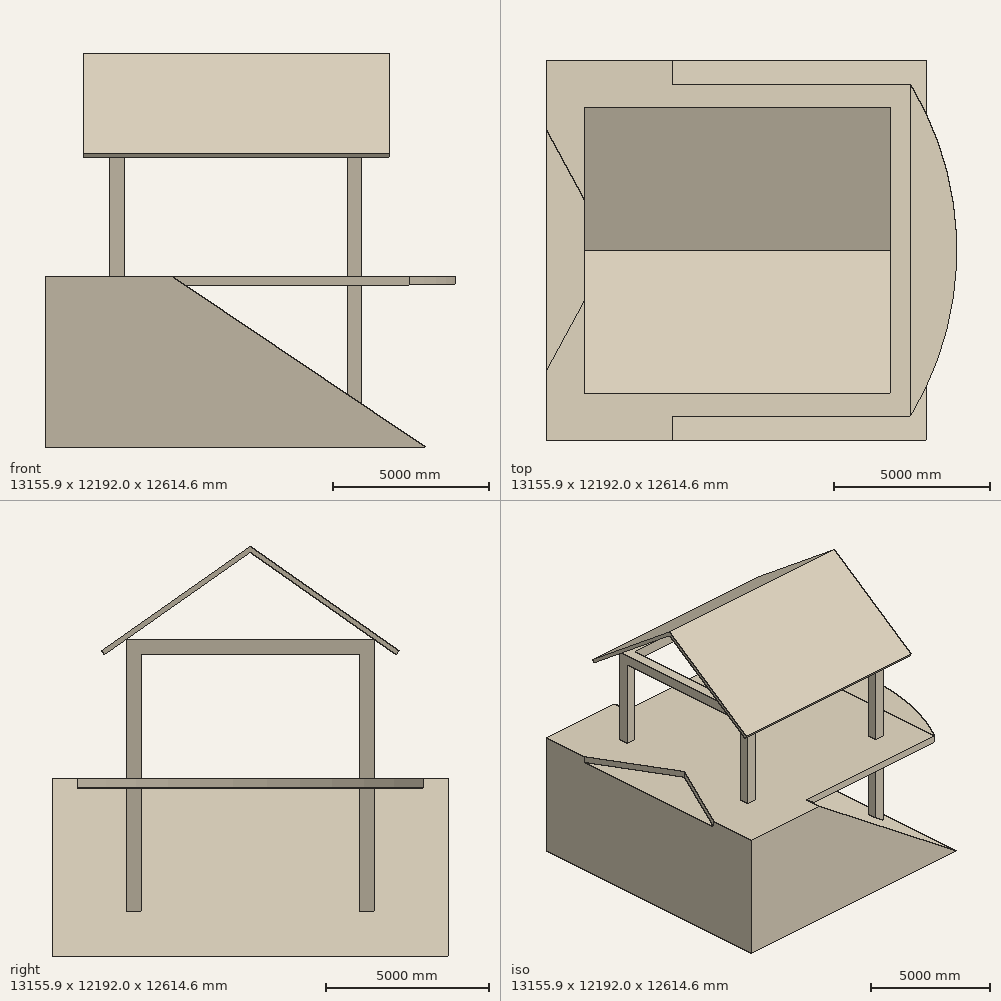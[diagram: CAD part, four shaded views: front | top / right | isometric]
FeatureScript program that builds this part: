
annotation { "Feature Type Name" : "Feature", "Feature Type Description" : "" }
export const myFeature = defineFeature(function(context is Context, id is Id, definition is map)
    precondition{}
    {
        {
            var Q0;
            Q0=qCreatedBy(makeId("Front.planeOp"),FACE);
            var sketch = newSketch(context, id + "F0", { "sketchPlane" : qUnion([Q0])});
            skLineSegment(sketch, "E0", {"start": v(-4044.06, 0) * mm, "end": v(0, 0) * mm});
            skLineSegment(sketch, "E1", {"start": v(0, 0) * mm, "end": v(8147.94, -5486.4) * mm});
            skLineSegment(sketch, "E2", {"start": v(8147.94, -5486.4) * mm, "end": v(-4044.06, -5486.4) * mm});
            skLineSegment(sketch, "E3", {"start": v(-4044.06, -5486.4) * mm, "end": v(-4044.06, 0) * mm});
            skSolve(sketch);
        }
        {
            var Q0;
            Q0=qSketchRegion(id+"F0",true);
            extrude(context, id + "F1", {"entities" : qUnion([Q0]), "endBound" : BoundingType.SYMMETRIC, "depth" : 12192 * mm});
        }
        {
            var Q0;
            Q0=qCreatedBy(makeId("Top.planeOp"),FACE);
            var sketch = newSketch(context, id + "F2", { "sketchPlane" : qUnion([Q0])});
            skLineSegment(sketch, "E4.bottom", {"start": v(-3048, 5334) * mm, "end": v(7620, 5334) * mm});
            skLineSegment(sketch, "E4.top", {"start": v(-3048, -5334) * mm, "end": v(7620, -5334) * mm});
            skLineSegment(sketch, "E4.left", {"start": v(-3048, 5334) * mm, "end": v(-3048, -5334) * mm});
            skLineSegment(sketch, "E4.right", {"start": v(7620, 5334) * mm, "end": v(7620, -5334) * mm});
            skSolve(sketch);
        }
        {
            var Q0;
            Q0=qSketchRegion(id+"F2",true);
            extrude(context, id + "F3", {"entities" : qUnion([Q0]), "operationType" : NewBodyOperationType.ADD, "oppositeDirection" : true, "depth" : 304.8 * mm});
        }
        {
            var Q0;
            Q0=makeQuery(id+"F3.boolean.opBoolean","MERGE",FACE,{"derivedFrom":[makeQuery(id+"F1.opExtrude","SWEPT_FACE",FACE,{"disambiguationData":[OSD([sQuery(id+"F0.wireOp",EDGE,"E0")])]}),makeQuery(id+"F3.opExtrude","CAP_FACE",FACE,{"disambiguationData":[OSD([sQuery(id+"F2.wireOp",EDGE,"E4.bottom"),sQuery(id+"F2.wireOp",EDGE,"E4.top"),sQuery(id+"F2.wireOp",EDGE,"E4.left"),sQuery(id+"F2.wireOp",EDGE,"E4.right")])],"isStart":true})]});
            var sketch = newSketch(context, id + "F4", { "sketchPlane" : qUnion([Q0])});
            skLineSegment(sketch, "E5.bottom", {"start": v(5638.8, 3810) * mm, "end": v(6096, 3810) * mm});
            skLineSegment(sketch, "E5.top", {"start": v(5638.8, 3352.8) * mm, "end": v(6096, 3352.8) * mm});
            skLineSegment(sketch, "E5.left", {"start": v(5638.8, 3810) * mm, "end": v(5638.8, 3352.8) * mm});
            skLineSegment(sketch, "E5.right", {"start": v(6096, 3810) * mm, "end": v(6096, 3352.8) * mm});
            skLineSegment(sketch, "E6.bottom", {"start": v(5638.8, -3352.8) * mm, "end": v(6096, -3352.8) * mm});
            skLineSegment(sketch, "E6.top", {"start": v(5638.8, -3810) * mm, "end": v(6096, -3810) * mm});
            skLineSegment(sketch, "E6.left", {"start": v(5638.8, -3352.8) * mm, "end": v(5638.8, -3810) * mm});
            skLineSegment(sketch, "E6.right", {"start": v(6096, -3352.8) * mm, "end": v(6096, -3810) * mm});
            skLineSegment(sketch, "E7.bottom", {"start": v(-1981.2, -3352.8) * mm, "end": v(-1524, -3352.8) * mm});
            skLineSegment(sketch, "E7.top", {"start": v(-1981.2, -3810) * mm, "end": v(-1524, -3810) * mm});
            skLineSegment(sketch, "E7.left", {"start": v(-1981.2, -3352.8) * mm, "end": v(-1981.2, -3810) * mm});
            skLineSegment(sketch, "E7.right", {"start": v(-1524, -3352.8) * mm, "end": v(-1524, -3810) * mm});
            skLineSegment(sketch, "E8.bottom", {"start": v(-1981.2, 3352.8) * mm, "end": v(-1524, 3352.8) * mm});
            skLineSegment(sketch, "E8.top", {"start": v(-1981.2, 3810) * mm, "end": v(-1524, 3810) * mm});
            skLineSegment(sketch, "E8.left", {"start": v(-1981.2, 3352.8) * mm, "end": v(-1981.2, 3810) * mm});
            skLineSegment(sketch, "E8.right", {"start": v(-1524, 3352.8) * mm, "end": v(-1524, 3810) * mm});
            skSolve(sketch);
        }
        {
            var Q0;
            Q0=qSketchRegion(id+"F4",true);
            extrude(context, id + "F5", {"entities" : qUnion([Q0]), "operationType" : NewBodyOperationType.ADD, "endBound" : BoundingType.SYMMETRIC, "depth" : 8534.4 * mm});
        }
        {
            var Q0;
            Q0=makeQuery(id+"F5.opExtrude","SWEPT_FACE",FACE,{"disambiguationData":[OSD([sQuery(id+"F4.wireOp",EDGE,"E8.bottom")])]});
            var sketch = newSketch(context, id + "F6", { "sketchPlane" : qUnion([Q0])});
            skLineSegment(sketch, "E9.bottom", {"start": v(-1981.2, 4267.2) * mm, "end": v(-1524, 4267.2) * mm});
            skLineSegment(sketch, "E9.top", {"start": v(-1981.2, 3810) * mm, "end": v(-1524, 3810) * mm});
            skLineSegment(sketch, "E9.left", {"start": v(-1981.2, 4267.2) * mm, "end": v(-1981.2, 3810) * mm});
            skLineSegment(sketch, "E9.right", {"start": v(-1524, 4267.2) * mm, "end": v(-1524, 3810) * mm});
            skLineSegment(sketch, "E10.bottom", {"start": v(6096, 4267.2) * mm, "end": v(5638.8, 4267.2) * mm});
            skLineSegment(sketch, "E10.top", {"start": v(6096, 3810) * mm, "end": v(5638.8, 3810) * mm});
            skLineSegment(sketch, "E10.left", {"start": v(6096, 4267.2) * mm, "end": v(6096, 3810) * mm});
            skLineSegment(sketch, "E10.right", {"start": v(5638.8, 4267.2) * mm, "end": v(5638.8, 3810) * mm});
            skSolve(sketch);
        }
        {
            var Q0;
            Q0=qSketchRegion(id+"F6",true);
            extrude(context, id + "F7", {"entities" : qUnion([Q0]), "operationType" : NewBodyOperationType.ADD, "depth" : 7112 * mm});
        }
        {
            var Q0;
            {var subQ2=sQuery(id+"F4.wireOp",EDGE,"E6.left");var subQ4=makeQuery(id+"F1.opExtrude","SWEPT_FACE",FACE,{"disambiguationData":[OSD([sQuery(id+"F0.wireOp",EDGE,"E0")])]});var subQ6=sQuery(id+"F4.wireOp",EDGE,"E5.left");Q0=makeQuery(id+"F7.boolean.opBoolean","MERGE",FACE,{"derivedFrom":[makeQuery(id+"F5.boolean.opBoolean","SPLIT",FACE,{"disambiguationData":[TD([subQ4])],"derivedFrom":makeQuery(id+"F5.opExtrude","SWEPT_FACE",FACE,{"disambiguationData":[OSD([subQ6])]})}),makeQuery(id+"F5.boolean.opBoolean","SPLIT",FACE,{"disambiguationData":[TD([subQ4])],"derivedFrom":makeQuery(id+"F5.opExtrude","SWEPT_FACE",FACE,{"disambiguationData":[OSD([subQ2])]})}),makeQuery(id+"F7.opExtrude","SWEPT_FACE",FACE,{"disambiguationData":[OSD([sQuery(id+"F6.wireOp",EDGE,"E10.right")])]})]});}
            var sketch = newSketch(context, id + "F8", { "sketchPlane" : qUnion([Q0])});
            skLineSegment(sketch, "E11.bottom", {"start": v(-3810, 4267.2) * mm, "end": v(-3352.8, 4267.2) * mm});
            skLineSegment(sketch, "E11.top", {"start": v(-3810, 3810) * mm, "end": v(-3352.8, 3810) * mm});
            skLineSegment(sketch, "E11.left", {"start": v(-3810, 4267.2) * mm, "end": v(-3810, 3810) * mm});
            skLineSegment(sketch, "E11.right", {"start": v(-3352.8, 4267.2) * mm, "end": v(-3352.8, 3810) * mm});
            skLineSegment(sketch, "E12.bottom", {"start": v(3352.8, 3810) * mm, "end": v(3810, 3810) * mm});
            skLineSegment(sketch, "E12.top", {"start": v(3352.8, 4267.2) * mm, "end": v(3810, 4267.2) * mm});
            skLineSegment(sketch, "E12.left", {"start": v(3352.8, 3810) * mm, "end": v(3352.8, 4267.2) * mm});
            skLineSegment(sketch, "E12.right", {"start": v(3810, 3810) * mm, "end": v(3810, 4267.2) * mm});
            skSolve(sketch);
        }
        {
            var Q0;
            Q0=qSketchRegion(id+"F8",true);
            extrude(context, id + "F9", {"entities" : qUnion([Q0]), "operationType" : NewBodyOperationType.ADD, "depth" : 7594.6 * mm});
        }
        {
            var Q0;
            Q0=qCreatedBy(makeId("Right.planeOp"),FACE);
            var sketch = newSketch(context, id + "F10", { "sketchPlane" : qUnion([Q0])});
            skLineSegment(sketch, "E13", {"start": v(-3810, 4267.2) * mm, "end": v(0, 6942) * mm});
            skLineSegment(sketch, "E14", {"start": v(0, 6942) * mm, "end": v(0, 7128.2) * mm});
            skLineSegment(sketch, "E15", {"start": v(0, 7128.2) * mm, "end": v(-4576.9, 3915) * mm});
            skLineSegment(sketch, "E16", {"start": v(-4576.9, 3915) * mm, "end": v(-4489.34, 3790.27) * mm});
            skLineSegment(sketch, "E17", {"start": v(-4489.34, 3790.27) * mm, "end": v(-3810, 4267.2) * mm});
            skLineSegment(sketch, "E18.MirrorCS", {"start": v(0, 7128.2) * mm, "end": v(4576.9, 3915) * mm});
            skLineSegment(sketch, "E19.MirrorCS", {"start": v(3810, 4267.2) * mm, "end": v(0, 6942) * mm});
            skLineSegment(sketch, "E20.MirrorCS", {"start": v(4489.34, 3790.27) * mm, "end": v(3810, 4267.2) * mm});
            skLineSegment(sketch, "E21.MirrorCS", {"start": v(4576.9, 3915) * mm, "end": v(4489.34, 3790.27) * mm});
            skSolve(sketch);
        }
        {
            var Q0;
            Q0=qSketchRegion(id+"F10",true);
            extrude(context, id + "F11", {"entities" : qUnion([Q0]), "depth" : 6985 * mm, "hasSecondDirection" : true, "secondDirectionOppositeDirection" : true, "secondDirectionDepth" : 2819.4 * mm});
        }
        {
            var Q0;
            Q0=makeQuery(id+"F3.opExtrude","SWEPT_FACE",FACE,{"disambiguationData":[OSD([sQuery(id+"F2.wireOp",EDGE,"E4.right")])]});
            var sketch = newSketch(context, id + "F12", { "sketchPlane" : qUnion([Q0])});
            skLineSegment(sketch, "E22.bottom", {"start": v(-5334, -304.8) * mm, "end": v(-5283.2, -304.8) * mm});
            skLineSegment(sketch, "E22.top", {"start": v(-5334, 914.4) * mm, "end": v(-5283.2, 914.4) * mm});
            skLineSegment(sketch, "E22.left", {"start": v(-5334, -304.8) * mm, "end": v(-5334, 914.4) * mm});
            skLineSegment(sketch, "E22.right", {"start": v(-5283.2, -304.8) * mm, "end": v(-5283.2, 914.4) * mm});
            skLineSegment(sketch, "E23.1.0.0", {"start": v(-5060.95, -304.8) * mm, "end": v(-5060.95, 914.4) * mm});
            skLineSegment(sketch, "E23.1.0.1", {"start": v(-5010.15, -304.8) * mm, "end": v(-5010.15, 914.4) * mm});
            skLineSegment(sketch, "E23.1.0.2", {"start": v(-5060.95, 914.4) * mm, "end": v(-5010.15, 914.4) * mm});
            skLineSegment(sketch, "E23.1.0.3", {"start": v(-5060.95, -304.8) * mm, "end": v(-5010.15, -304.8) * mm});
            skLineSegment(sketch, "E23.2.0.0", {"start": v(-4787.9, -304.8) * mm, "end": v(-4787.9, 914.4) * mm});
            skLineSegment(sketch, "E23.2.0.1", {"start": v(-4737.1, -304.8) * mm, "end": v(-4737.1, 914.4) * mm});
            skLineSegment(sketch, "E23.2.0.2", {"start": v(-4787.9, 914.4) * mm, "end": v(-4737.1, 914.4) * mm});
            skLineSegment(sketch, "E23.2.0.3", {"start": v(-4787.9, -304.8) * mm, "end": v(-4737.1, -304.8) * mm});
            skLineSegment(sketch, "E23.3.0.0", {"start": v(-4514.85, -304.8) * mm, "end": v(-4514.85, 914.4) * mm});
            skLineSegment(sketch, "E23.3.0.1", {"start": v(-4464.05, -304.8) * mm, "end": v(-4464.05, 914.4) * mm});
            skLineSegment(sketch, "E23.3.0.2", {"start": v(-4514.85, 914.4) * mm, "end": v(-4464.05, 914.4) * mm});
            skLineSegment(sketch, "E23.3.0.3", {"start": v(-4514.85, -304.8) * mm, "end": v(-4464.05, -304.8) * mm});
            skLineSegment(sketch, "E23.4.0.0", {"start": v(-4241.8, -304.8) * mm, "end": v(-4241.8, 914.4) * mm});
            skLineSegment(sketch, "E23.4.0.1", {"start": v(-4191, -304.8) * mm, "end": v(-4191, 914.4) * mm});
            skLineSegment(sketch, "E23.4.0.2", {"start": v(-4241.8, 914.4) * mm, "end": v(-4191, 914.4) * mm});
            skLineSegment(sketch, "E23.4.0.3", {"start": v(-4241.8, -304.8) * mm, "end": v(-4191, -304.8) * mm});
            skLineSegment(sketch, "E23.5.0.0", {"start": v(-3968.75, -304.8) * mm, "end": v(-3968.75, 914.4) * mm});
            skLineSegment(sketch, "E23.5.0.1", {"start": v(-3917.95, -304.8) * mm, "end": v(-3917.95, 914.4) * mm});
            skLineSegment(sketch, "E23.5.0.2", {"start": v(-3968.75, 914.4) * mm, "end": v(-3917.95, 914.4) * mm});
            skLineSegment(sketch, "E23.5.0.3", {"start": v(-3968.75, -304.8) * mm, "end": v(-3917.95, -304.8) * mm});
            skLineSegment(sketch, "E23.6.0.0", {"start": v(-3695.7, -304.8) * mm, "end": v(-3695.7, 914.4) * mm});
            skLineSegment(sketch, "E23.6.0.1", {"start": v(-3644.9, -304.8) * mm, "end": v(-3644.9, 914.4) * mm});
            skLineSegment(sketch, "E23.6.0.2", {"start": v(-3695.7, 914.4) * mm, "end": v(-3644.9, 914.4) * mm});
            skLineSegment(sketch, "E23.6.0.3", {"start": v(-3695.7, -304.8) * mm, "end": v(-3644.9, -304.8) * mm});
            skLineSegment(sketch, "E23.7.0.0", {"start": v(-3422.65, -304.8) * mm, "end": v(-3422.65, 914.4) * mm});
            skLineSegment(sketch, "E23.7.0.1", {"start": v(-3371.85, -304.8) * mm, "end": v(-3371.85, 914.4) * mm});
            skLineSegment(sketch, "E23.7.0.2", {"start": v(-3422.65, 914.4) * mm, "end": v(-3371.85, 914.4) * mm});
            skLineSegment(sketch, "E23.7.0.3", {"start": v(-3422.65, -304.8) * mm, "end": v(-3371.85, -304.8) * mm});
            skLineSegment(sketch, "E23.8.0.0", {"start": v(-3149.6, -304.8) * mm, "end": v(-3149.6, 914.4) * mm});
            skLineSegment(sketch, "E23.8.0.1", {"start": v(-3098.8, -304.8) * mm, "end": v(-3098.8, 914.4) * mm});
            skLineSegment(sketch, "E23.8.0.2", {"start": v(-3149.6, 914.4) * mm, "end": v(-3098.8, 914.4) * mm});
            skLineSegment(sketch, "E23.8.0.3", {"start": v(-3149.6, -304.8) * mm, "end": v(-3098.8, -304.8) * mm});
            skLineSegment(sketch, "E23.9.0.0", {"start": v(-2876.55, -304.8) * mm, "end": v(-2876.55, 914.4) * mm});
            skLineSegment(sketch, "E23.9.0.1", {"start": v(-2825.75, -304.8) * mm, "end": v(-2825.75, 914.4) * mm});
            skLineSegment(sketch, "E23.9.0.2", {"start": v(-2876.55, 914.4) * mm, "end": v(-2825.75, 914.4) * mm});
            skLineSegment(sketch, "E23.9.0.3", {"start": v(-2876.55, -304.8) * mm, "end": v(-2825.75, -304.8) * mm});
            skLineSegment(sketch, "E23.10.0.0", {"start": v(-2603.5, -304.8) * mm, "end": v(-2603.5, 914.4) * mm});
            skLineSegment(sketch, "E23.10.0.1", {"start": v(-2552.7, -304.8) * mm, "end": v(-2552.7, 914.4) * mm});
            skLineSegment(sketch, "E23.10.0.2", {"start": v(-2603.5, 914.4) * mm, "end": v(-2552.7, 914.4) * mm});
            skLineSegment(sketch, "E23.10.0.3", {"start": v(-2603.5, -304.8) * mm, "end": v(-2552.7, -304.8) * mm});
            skLineSegment(sketch, "E23.11.0.0", {"start": v(-2330.45, -304.8) * mm, "end": v(-2330.45, 914.4) * mm});
            skLineSegment(sketch, "E23.11.0.1", {"start": v(-2279.65, -304.8) * mm, "end": v(-2279.65, 914.4) * mm});
            skLineSegment(sketch, "E23.11.0.2", {"start": v(-2330.45, 914.4) * mm, "end": v(-2279.65, 914.4) * mm});
            skLineSegment(sketch, "E23.11.0.3", {"start": v(-2330.45, -304.8) * mm, "end": v(-2279.65, -304.8) * mm});
            skLineSegment(sketch, "E23.12.0.0", {"start": v(-2057.4, -304.8) * mm, "end": v(-2057.4, 914.4) * mm});
            skLineSegment(sketch, "E23.12.0.1", {"start": v(-2006.6, -304.8) * mm, "end": v(-2006.6, 914.4) * mm});
            skLineSegment(sketch, "E23.12.0.2", {"start": v(-2057.4, 914.4) * mm, "end": v(-2006.6, 914.4) * mm});
            skLineSegment(sketch, "E23.12.0.3", {"start": v(-2057.4, -304.8) * mm, "end": v(-2006.6, -304.8) * mm});
            skLineSegment(sketch, "E23.13.0.0", {"start": v(-1784.35, -304.8) * mm, "end": v(-1784.35, 914.4) * mm});
            skLineSegment(sketch, "E23.13.0.1", {"start": v(-1733.55, -304.8) * mm, "end": v(-1733.55, 914.4) * mm});
            skLineSegment(sketch, "E23.13.0.2", {"start": v(-1784.35, 914.4) * mm, "end": v(-1733.55, 914.4) * mm});
            skLineSegment(sketch, "E23.13.0.3", {"start": v(-1784.35, -304.8) * mm, "end": v(-1733.55, -304.8) * mm});
            skLineSegment(sketch, "E23.14.0.0", {"start": v(-1511.3, -304.8) * mm, "end": v(-1511.3, 914.4) * mm});
            skLineSegment(sketch, "E23.14.0.1", {"start": v(-1460.5, -304.8) * mm, "end": v(-1460.5, 914.4) * mm});
            skLineSegment(sketch, "E23.14.0.2", {"start": v(-1511.3, 914.4) * mm, "end": v(-1460.5, 914.4) * mm});
            skLineSegment(sketch, "E23.14.0.3", {"start": v(-1511.3, -304.8) * mm, "end": v(-1460.5, -304.8) * mm});
            skLineSegment(sketch, "E23.15.0.0", {"start": v(-1238.25, -304.8) * mm, "end": v(-1238.25, 914.4) * mm});
            skLineSegment(sketch, "E23.15.0.1", {"start": v(-1187.45, -304.8) * mm, "end": v(-1187.45, 914.4) * mm});
            skLineSegment(sketch, "E23.15.0.2", {"start": v(-1238.25, 914.4) * mm, "end": v(-1187.45, 914.4) * mm});
            skLineSegment(sketch, "E23.15.0.3", {"start": v(-1238.25, -304.8) * mm, "end": v(-1187.45, -304.8) * mm});
            skLineSegment(sketch, "E23.16.0.0", {"start": v(-965.2, -304.8) * mm, "end": v(-965.2, 914.4) * mm});
            skLineSegment(sketch, "E23.16.0.1", {"start": v(-914.4, -304.8) * mm, "end": v(-914.4, 914.4) * mm});
            skLineSegment(sketch, "E23.16.0.2", {"start": v(-965.2, 914.4) * mm, "end": v(-914.4, 914.4) * mm});
            skLineSegment(sketch, "E23.16.0.3", {"start": v(-965.2, -304.8) * mm, "end": v(-914.4, -304.8) * mm});
            skLineSegment(sketch, "E23.17.0.0", {"start": v(-692.15, -304.8) * mm, "end": v(-692.15, 914.4) * mm});
            skLineSegment(sketch, "E23.17.0.1", {"start": v(-641.35, -304.8) * mm, "end": v(-641.35, 914.4) * mm});
            skLineSegment(sketch, "E23.17.0.2", {"start": v(-692.15, 914.4) * mm, "end": v(-641.35, 914.4) * mm});
            skLineSegment(sketch, "E23.17.0.3", {"start": v(-692.15, -304.8) * mm, "end": v(-641.35, -304.8) * mm});
            skLineSegment(sketch, "E23.18.0.0", {"start": v(-419.1, -304.8) * mm, "end": v(-419.1, 914.4) * mm});
            skLineSegment(sketch, "E23.18.0.1", {"start": v(-368.3, -304.8) * mm, "end": v(-368.3, 914.4) * mm});
            skLineSegment(sketch, "E23.18.0.2", {"start": v(-419.1, 914.4) * mm, "end": v(-368.3, 914.4) * mm});
            skLineSegment(sketch, "E23.18.0.3", {"start": v(-419.1, -304.8) * mm, "end": v(-368.3, -304.8) * mm});
            skLineSegment(sketch, "E23.19.0.0", {"start": v(-146.05, -304.8) * mm, "end": v(-146.05, 914.4) * mm});
            skLineSegment(sketch, "E23.19.0.1", {"start": v(-95.25, -304.8) * mm, "end": v(-95.25, 914.4) * mm});
            skLineSegment(sketch, "E23.19.0.2", {"start": v(-146.05, 914.4) * mm, "end": v(-95.25, 914.4) * mm});
            skLineSegment(sketch, "E23.19.0.3", {"start": v(-146.05, -304.8) * mm, "end": v(-95.25, -304.8) * mm});
            skLineSegment(sketch, "E23.20.0.0", {"start": v(127, -304.8) * mm, "end": v(127, 914.4) * mm});
            skLineSegment(sketch, "E23.20.0.1", {"start": v(177.8, -304.8) * mm, "end": v(177.8, 914.4) * mm});
            skLineSegment(sketch, "E23.20.0.2", {"start": v(127, 914.4) * mm, "end": v(177.8, 914.4) * mm});
            skLineSegment(sketch, "E23.20.0.3", {"start": v(127, -304.8) * mm, "end": v(177.8, -304.8) * mm});
            skLineSegment(sketch, "E23.21.0.0", {"start": v(400.05, -304.8) * mm, "end": v(400.05, 914.4) * mm});
            skLineSegment(sketch, "E23.21.0.1", {"start": v(450.85, -304.8) * mm, "end": v(450.85, 914.4) * mm});
            skLineSegment(sketch, "E23.21.0.2", {"start": v(400.05, 914.4) * mm, "end": v(450.85, 914.4) * mm});
            skLineSegment(sketch, "E23.21.0.3", {"start": v(400.05, -304.8) * mm, "end": v(450.85, -304.8) * mm});
            skLineSegment(sketch, "E23.22.0.0", {"start": v(673.1, -304.8) * mm, "end": v(673.1, 914.4) * mm});
            skLineSegment(sketch, "E23.22.0.1", {"start": v(723.9, -304.8) * mm, "end": v(723.9, 914.4) * mm});
            skLineSegment(sketch, "E23.22.0.2", {"start": v(673.1, 914.4) * mm, "end": v(723.9, 914.4) * mm});
            skLineSegment(sketch, "E23.22.0.3", {"start": v(673.1, -304.8) * mm, "end": v(723.9, -304.8) * mm});
            skLineSegment(sketch, "E23.23.0.0", {"start": v(946.15, -304.8) * mm, "end": v(946.15, 914.4) * mm});
            skLineSegment(sketch, "E23.23.0.1", {"start": v(996.95, -304.8) * mm, "end": v(996.95, 914.4) * mm});
            skLineSegment(sketch, "E23.23.0.2", {"start": v(946.15, 914.4) * mm, "end": v(996.95, 914.4) * mm});
            skLineSegment(sketch, "E23.23.0.3", {"start": v(946.15, -304.8) * mm, "end": v(996.95, -304.8) * mm});
            skLineSegment(sketch, "E23.24.0.0", {"start": v(1219.2, -304.8) * mm, "end": v(1219.2, 914.4) * mm});
            skLineSegment(sketch, "E23.24.0.1", {"start": v(1270, -304.8) * mm, "end": v(1270, 914.4) * mm});
            skLineSegment(sketch, "E23.24.0.2", {"start": v(1219.2, 914.4) * mm, "end": v(1270, 914.4) * mm});
            skLineSegment(sketch, "E23.24.0.3", {"start": v(1219.2, -304.8) * mm, "end": v(1270, -304.8) * mm});
            skLineSegment(sketch, "E23.25.0.0", {"start": v(1492.25, -304.8) * mm, "end": v(1492.25, 914.4) * mm});
            skLineSegment(sketch, "E23.25.0.1", {"start": v(1543.05, -304.8) * mm, "end": v(1543.05, 914.4) * mm});
            skLineSegment(sketch, "E23.25.0.2", {"start": v(1492.25, 914.4) * mm, "end": v(1543.05, 914.4) * mm});
            skLineSegment(sketch, "E23.25.0.3", {"start": v(1492.25, -304.8) * mm, "end": v(1543.05, -304.8) * mm});
            skLineSegment(sketch, "E23.26.0.0", {"start": v(1765.3, -304.8) * mm, "end": v(1765.3, 914.4) * mm});
            skLineSegment(sketch, "E23.26.0.1", {"start": v(1816.1, -304.8) * mm, "end": v(1816.1, 914.4) * mm});
            skLineSegment(sketch, "E23.26.0.2", {"start": v(1765.3, 914.4) * mm, "end": v(1816.1, 914.4) * mm});
            skLineSegment(sketch, "E23.26.0.3", {"start": v(1765.3, -304.8) * mm, "end": v(1816.1, -304.8) * mm});
            skLineSegment(sketch, "E23.27.0.0", {"start": v(2038.35, -304.8) * mm, "end": v(2038.35, 914.4) * mm});
            skLineSegment(sketch, "E23.27.0.1", {"start": v(2089.15, -304.8) * mm, "end": v(2089.15, 914.4) * mm});
            skLineSegment(sketch, "E23.27.0.2", {"start": v(2038.35, 914.4) * mm, "end": v(2089.15, 914.4) * mm});
            skLineSegment(sketch, "E23.27.0.3", {"start": v(2038.35, -304.8) * mm, "end": v(2089.15, -304.8) * mm});
            skLineSegment(sketch, "E23.28.0.0", {"start": v(2311.4, -304.8) * mm, "end": v(2311.4, 914.4) * mm});
            skLineSegment(sketch, "E23.28.0.1", {"start": v(2362.2, -304.8) * mm, "end": v(2362.2, 914.4) * mm});
            skLineSegment(sketch, "E23.28.0.2", {"start": v(2311.4, 914.4) * mm, "end": v(2362.2, 914.4) * mm});
            skLineSegment(sketch, "E23.28.0.3", {"start": v(2311.4, -304.8) * mm, "end": v(2362.2, -304.8) * mm});
            skLineSegment(sketch, "E23.29.0.0", {"start": v(2584.45, -304.8) * mm, "end": v(2584.45, 914.4) * mm});
            skLineSegment(sketch, "E23.29.0.1", {"start": v(2635.25, -304.8) * mm, "end": v(2635.25, 914.4) * mm});
            skLineSegment(sketch, "E23.29.0.2", {"start": v(2584.45, 914.4) * mm, "end": v(2635.25, 914.4) * mm});
            skLineSegment(sketch, "E23.29.0.3", {"start": v(2584.45, -304.8) * mm, "end": v(2635.25, -304.8) * mm});
            skLineSegment(sketch, "E23.30.0.0", {"start": v(2857.5, -304.8) * mm, "end": v(2857.5, 914.4) * mm});
            skLineSegment(sketch, "E23.30.0.1", {"start": v(2908.3, -304.8) * mm, "end": v(2908.3, 914.4) * mm});
            skLineSegment(sketch, "E23.30.0.2", {"start": v(2857.5, 914.4) * mm, "end": v(2908.3, 914.4) * mm});
            skLineSegment(sketch, "E23.30.0.3", {"start": v(2857.5, -304.8) * mm, "end": v(2908.3, -304.8) * mm});
            skLineSegment(sketch, "E23.31.0.0", {"start": v(3130.55, -304.8) * mm, "end": v(3130.55, 914.4) * mm});
            skLineSegment(sketch, "E23.31.0.1", {"start": v(3181.35, -304.8) * mm, "end": v(3181.35, 914.4) * mm});
            skLineSegment(sketch, "E23.31.0.2", {"start": v(3130.55, 914.4) * mm, "end": v(3181.35, 914.4) * mm});
            skLineSegment(sketch, "E23.31.0.3", {"start": v(3130.55, -304.8) * mm, "end": v(3181.35, -304.8) * mm});
            skLineSegment(sketch, "E23.32.0.0", {"start": v(3403.6, -304.8) * mm, "end": v(3403.6, 914.4) * mm});
            skLineSegment(sketch, "E23.32.0.1", {"start": v(3454.4, -304.8) * mm, "end": v(3454.4, 914.4) * mm});
            skLineSegment(sketch, "E23.32.0.2", {"start": v(3403.6, 914.4) * mm, "end": v(3454.4, 914.4) * mm});
            skLineSegment(sketch, "E23.32.0.3", {"start": v(3403.6, -304.8) * mm, "end": v(3454.4, -304.8) * mm});
            skLineSegment(sketch, "E23.33.0.0", {"start": v(3676.65, -304.8) * mm, "end": v(3676.65, 914.4) * mm});
            skLineSegment(sketch, "E23.33.0.1", {"start": v(3727.45, -304.8) * mm, "end": v(3727.45, 914.4) * mm});
            skLineSegment(sketch, "E23.33.0.2", {"start": v(3676.65, 914.4) * mm, "end": v(3727.45, 914.4) * mm});
            skLineSegment(sketch, "E23.33.0.3", {"start": v(3676.65, -304.8) * mm, "end": v(3727.45, -304.8) * mm});
            skLineSegment(sketch, "E23.34.0.0", {"start": v(3949.7, -304.8) * mm, "end": v(3949.7, 914.4) * mm});
            skLineSegment(sketch, "E23.34.0.1", {"start": v(4000.5, -304.8) * mm, "end": v(4000.5, 914.4) * mm});
            skLineSegment(sketch, "E23.34.0.2", {"start": v(3949.7, 914.4) * mm, "end": v(4000.5, 914.4) * mm});
            skLineSegment(sketch, "E23.34.0.3", {"start": v(3949.7, -304.8) * mm, "end": v(4000.5, -304.8) * mm});
            skLineSegment(sketch, "E23.35.0.0", {"start": v(4222.75, -304.8) * mm, "end": v(4222.75, 914.4) * mm});
            skLineSegment(sketch, "E23.35.0.1", {"start": v(4273.55, -304.8) * mm, "end": v(4273.55, 914.4) * mm});
            skLineSegment(sketch, "E23.35.0.2", {"start": v(4222.75, 914.4) * mm, "end": v(4273.55, 914.4) * mm});
            skLineSegment(sketch, "E23.35.0.3", {"start": v(4222.75, -304.8) * mm, "end": v(4273.55, -304.8) * mm});
            skLineSegment(sketch, "E23.36.0.0", {"start": v(4495.8, -304.8) * mm, "end": v(4495.8, 914.4) * mm});
            skLineSegment(sketch, "E23.36.0.1", {"start": v(4546.6, -304.8) * mm, "end": v(4546.6, 914.4) * mm});
            skLineSegment(sketch, "E23.36.0.2", {"start": v(4495.8, 914.4) * mm, "end": v(4546.6, 914.4) * mm});
            skLineSegment(sketch, "E23.36.0.3", {"start": v(4495.8, -304.8) * mm, "end": v(4546.6, -304.8) * mm});
            skLineSegment(sketch, "E23.37.0.0", {"start": v(4768.85, -304.8) * mm, "end": v(4768.85, 914.4) * mm});
            skLineSegment(sketch, "E23.37.0.1", {"start": v(4819.65, -304.8) * mm, "end": v(4819.65, 914.4) * mm});
            skLineSegment(sketch, "E23.37.0.2", {"start": v(4768.85, 914.4) * mm, "end": v(4819.65, 914.4) * mm});
            skLineSegment(sketch, "E23.37.0.3", {"start": v(4768.85, -304.8) * mm, "end": v(4819.65, -304.8) * mm});
            skLineSegment(sketch, "E23.38.0.0", {"start": v(5041.9, -304.8) * mm, "end": v(5041.9, 914.4) * mm});
            skLineSegment(sketch, "E23.38.0.1", {"start": v(5092.7, -304.8) * mm, "end": v(5092.7, 914.4) * mm});
            skLineSegment(sketch, "E23.38.0.2", {"start": v(5041.9, 914.4) * mm, "end": v(5092.7, 914.4) * mm});
            skLineSegment(sketch, "E23.38.0.3", {"start": v(5041.9, -304.8) * mm, "end": v(5092.7, -304.8) * mm});
            skLineSegment(sketch, "E23.39.0.0", {"start": v(5314.95, -304.8) * mm, "end": v(5314.95, 914.4) * mm});
            skLineSegment(sketch, "E23.39.0.1", {"start": v(5365.75, -304.8) * mm, "end": v(5365.75, 914.4) * mm});
            skLineSegment(sketch, "E23.39.0.2", {"start": v(5314.95, 914.4) * mm, "end": v(5365.75, 914.4) * mm});
            skLineSegment(sketch, "E23.39.0.3", {"start": v(5314.95, -304.8) * mm, "end": v(5365.75, -304.8) * mm});
            skLineSegment(sketch, "E23.direction1", {"start": v(-5334, -304.8) * mm, "end": v(-5060.95, -304.8) * mm, "construction": true});
            skSolve(sketch);
        }
        {
            var Q0;
            Q0=makeQuery(id+"F85cZeWVdczHBdZ_2.boolean.opBoolean","MERGE",FACE,{"derivedFrom":[makeQuery(id+"F3.opExtrude","SWEPT_FACE",FACE,{"disambiguationData":[OSD([sQuery(id+"F2.wireOp",EDGE,"E4.top")])]}),makeQuery(id+"F85cZeWVdczHBdZ_2.opExtrude","SWEPT_FACE",FACE,{"disambiguationData":[OSD([sQuery(id+"F12.wireOp",EDGE,"E22.left")])]})]});
            var sketch = newSketch(context, id + "F13", { "sketchPlane" : qUnion([Q0])});
            skLineSegment(sketch, "E24.bottom", {"start": v(7670.8, -304.8) * mm, "end": v(7620, -304.8) * mm});
            skLineSegment(sketch, "E24.top", {"start": v(7670.8, 914.4) * mm, "end": v(7620, 914.4) * mm});
            skLineSegment(sketch, "E24.left", {"start": v(7670.8, -304.8) * mm, "end": v(7670.8, 914.4) * mm});
            skLineSegment(sketch, "E24.right", {"start": v(7620, -304.8) * mm, "end": v(7620, 914.4) * mm});
            skLineSegment(sketch, "E25.1.0.0", {"start": v(7346.95, -304.8) * mm, "end": v(7346.95, 914.4) * mm});
            skLineSegment(sketch, "E25.1.0.1", {"start": v(7397.75, -304.8) * mm, "end": v(7397.75, 914.4) * mm});
            skLineSegment(sketch, "E25.1.0.2", {"start": v(7397.75, 914.4) * mm, "end": v(7346.95, 914.4) * mm});
            skLineSegment(sketch, "E25.1.0.3", {"start": v(7397.75, -304.8) * mm, "end": v(7346.95, -304.8) * mm});
            skLineSegment(sketch, "E25.2.0.0", {"start": v(7073.9, -304.8) * mm, "end": v(7073.9, 914.4) * mm});
            skLineSegment(sketch, "E25.2.0.1", {"start": v(7124.7, -304.8) * mm, "end": v(7124.7, 914.4) * mm});
            skLineSegment(sketch, "E25.2.0.2", {"start": v(7124.7, 914.4) * mm, "end": v(7073.9, 914.4) * mm});
            skLineSegment(sketch, "E25.2.0.3", {"start": v(7124.7, -304.8) * mm, "end": v(7073.9, -304.8) * mm});
            skLineSegment(sketch, "E25.3.0.0", {"start": v(6800.85, -304.8) * mm, "end": v(6800.85, 914.4) * mm});
            skLineSegment(sketch, "E25.3.0.1", {"start": v(6851.65, -304.8) * mm, "end": v(6851.65, 914.4) * mm});
            skLineSegment(sketch, "E25.3.0.2", {"start": v(6851.65, 914.4) * mm, "end": v(6800.85, 914.4) * mm});
            skLineSegment(sketch, "E25.3.0.3", {"start": v(6851.65, -304.8) * mm, "end": v(6800.85, -304.8) * mm});
            skLineSegment(sketch, "E25.4.0.0", {"start": v(6527.8, -304.8) * mm, "end": v(6527.8, 914.4) * mm});
            skLineSegment(sketch, "E25.4.0.1", {"start": v(6578.6, -304.8) * mm, "end": v(6578.6, 914.4) * mm});
            skLineSegment(sketch, "E25.4.0.2", {"start": v(6578.6, 914.4) * mm, "end": v(6527.8, 914.4) * mm});
            skLineSegment(sketch, "E25.4.0.3", {"start": v(6578.6, -304.8) * mm, "end": v(6527.8, -304.8) * mm});
            skLineSegment(sketch, "E25.5.0.0", {"start": v(6254.75, -304.8) * mm, "end": v(6254.75, 914.4) * mm});
            skLineSegment(sketch, "E25.5.0.1", {"start": v(6305.55, -304.8) * mm, "end": v(6305.55, 914.4) * mm});
            skLineSegment(sketch, "E25.5.0.2", {"start": v(6305.55, 914.4) * mm, "end": v(6254.75, 914.4) * mm});
            skLineSegment(sketch, "E25.5.0.3", {"start": v(6305.55, -304.8) * mm, "end": v(6254.75, -304.8) * mm});
            skLineSegment(sketch, "E25.6.0.0", {"start": v(5981.7, -304.8) * mm, "end": v(5981.7, 914.4) * mm});
            skLineSegment(sketch, "E25.6.0.1", {"start": v(6032.5, -304.8) * mm, "end": v(6032.5, 914.4) * mm});
            skLineSegment(sketch, "E25.6.0.2", {"start": v(6032.5, 914.4) * mm, "end": v(5981.7, 914.4) * mm});
            skLineSegment(sketch, "E25.6.0.3", {"start": v(6032.5, -304.8) * mm, "end": v(5981.7, -304.8) * mm});
            skLineSegment(sketch, "E25.7.0.0", {"start": v(5708.65, -304.8) * mm, "end": v(5708.65, 914.4) * mm});
            skLineSegment(sketch, "E25.7.0.1", {"start": v(5759.45, -304.8) * mm, "end": v(5759.45, 914.4) * mm});
            skLineSegment(sketch, "E25.7.0.2", {"start": v(5759.45, 914.4) * mm, "end": v(5708.65, 914.4) * mm});
            skLineSegment(sketch, "E25.7.0.3", {"start": v(5759.45, -304.8) * mm, "end": v(5708.65, -304.8) * mm});
            skLineSegment(sketch, "E25.8.0.0", {"start": v(5435.6, -304.8) * mm, "end": v(5435.6, 914.4) * mm});
            skLineSegment(sketch, "E25.8.0.1", {"start": v(5486.4, -304.8) * mm, "end": v(5486.4, 914.4) * mm});
            skLineSegment(sketch, "E25.8.0.2", {"start": v(5486.4, 914.4) * mm, "end": v(5435.6, 914.4) * mm});
            skLineSegment(sketch, "E25.8.0.3", {"start": v(5486.4, -304.8) * mm, "end": v(5435.6, -304.8) * mm});
            skLineSegment(sketch, "E25.9.0.0", {"start": v(5162.55, -304.8) * mm, "end": v(5162.55, 914.4) * mm});
            skLineSegment(sketch, "E25.9.0.1", {"start": v(5213.35, -304.8) * mm, "end": v(5213.35, 914.4) * mm});
            skLineSegment(sketch, "E25.9.0.2", {"start": v(5213.35, 914.4) * mm, "end": v(5162.55, 914.4) * mm});
            skLineSegment(sketch, "E25.9.0.3", {"start": v(5213.35, -304.8) * mm, "end": v(5162.55, -304.8) * mm});
            skLineSegment(sketch, "E25.10.0.0", {"start": v(4889.5, -304.8) * mm, "end": v(4889.5, 914.4) * mm});
            skLineSegment(sketch, "E25.10.0.1", {"start": v(4940.3, -304.8) * mm, "end": v(4940.3, 914.4) * mm});
            skLineSegment(sketch, "E25.10.0.2", {"start": v(4940.3, 914.4) * mm, "end": v(4889.5, 914.4) * mm});
            skLineSegment(sketch, "E25.10.0.3", {"start": v(4940.3, -304.8) * mm, "end": v(4889.5, -304.8) * mm});
            skLineSegment(sketch, "E25.11.0.0", {"start": v(4616.45, -304.8) * mm, "end": v(4616.45, 914.4) * mm});
            skLineSegment(sketch, "E25.11.0.1", {"start": v(4667.25, -304.8) * mm, "end": v(4667.25, 914.4) * mm});
            skLineSegment(sketch, "E25.11.0.2", {"start": v(4667.25, 914.4) * mm, "end": v(4616.45, 914.4) * mm});
            skLineSegment(sketch, "E25.11.0.3", {"start": v(4667.25, -304.8) * mm, "end": v(4616.45, -304.8) * mm});
            skLineSegment(sketch, "E25.12.0.0", {"start": v(4343.4, -304.8) * mm, "end": v(4343.4, 914.4) * mm});
            skLineSegment(sketch, "E25.12.0.1", {"start": v(4394.2, -304.8) * mm, "end": v(4394.2, 914.4) * mm});
            skLineSegment(sketch, "E25.12.0.2", {"start": v(4394.2, 914.4) * mm, "end": v(4343.4, 914.4) * mm});
            skLineSegment(sketch, "E25.12.0.3", {"start": v(4394.2, -304.8) * mm, "end": v(4343.4, -304.8) * mm});
            skLineSegment(sketch, "E25.13.0.0", {"start": v(4070.35, -304.8) * mm, "end": v(4070.35, 914.4) * mm});
            skLineSegment(sketch, "E25.13.0.1", {"start": v(4121.15, -304.8) * mm, "end": v(4121.15, 914.4) * mm});
            skLineSegment(sketch, "E25.13.0.2", {"start": v(4121.15, 914.4) * mm, "end": v(4070.35, 914.4) * mm});
            skLineSegment(sketch, "E25.13.0.3", {"start": v(4121.15, -304.8) * mm, "end": v(4070.35, -304.8) * mm});
            skLineSegment(sketch, "E25.14.0.0", {"start": v(3797.3, -304.8) * mm, "end": v(3797.3, 914.4) * mm});
            skLineSegment(sketch, "E25.14.0.1", {"start": v(3848.1, -304.8) * mm, "end": v(3848.1, 914.4) * mm});
            skLineSegment(sketch, "E25.14.0.2", {"start": v(3848.1, 914.4) * mm, "end": v(3797.3, 914.4) * mm});
            skLineSegment(sketch, "E25.14.0.3", {"start": v(3848.1, -304.8) * mm, "end": v(3797.3, -304.8) * mm});
            skLineSegment(sketch, "E25.15.0.0", {"start": v(3524.25, -304.8) * mm, "end": v(3524.25, 914.4) * mm});
            skLineSegment(sketch, "E25.15.0.1", {"start": v(3575.05, -304.8) * mm, "end": v(3575.05, 914.4) * mm});
            skLineSegment(sketch, "E25.15.0.2", {"start": v(3575.05, 914.4) * mm, "end": v(3524.25, 914.4) * mm});
            skLineSegment(sketch, "E25.15.0.3", {"start": v(3575.05, -304.8) * mm, "end": v(3524.25, -304.8) * mm});
            skLineSegment(sketch, "E25.16.0.0", {"start": v(3251.2, -304.8) * mm, "end": v(3251.2, 914.4) * mm});
            skLineSegment(sketch, "E25.16.0.1", {"start": v(3302, -304.8) * mm, "end": v(3302, 914.4) * mm});
            skLineSegment(sketch, "E25.16.0.2", {"start": v(3302, 914.4) * mm, "end": v(3251.2, 914.4) * mm});
            skLineSegment(sketch, "E25.16.0.3", {"start": v(3302, -304.8) * mm, "end": v(3251.2, -304.8) * mm});
            skLineSegment(sketch, "E25.17.0.0", {"start": v(2978.15, -304.8) * mm, "end": v(2978.15, 914.4) * mm});
            skLineSegment(sketch, "E25.17.0.1", {"start": v(3028.95, -304.8) * mm, "end": v(3028.95, 914.4) * mm});
            skLineSegment(sketch, "E25.17.0.2", {"start": v(3028.95, 914.4) * mm, "end": v(2978.15, 914.4) * mm});
            skLineSegment(sketch, "E25.17.0.3", {"start": v(3028.95, -304.8) * mm, "end": v(2978.15, -304.8) * mm});
            skLineSegment(sketch, "E25.18.0.0", {"start": v(2705.1, -304.8) * mm, "end": v(2705.1, 914.4) * mm});
            skLineSegment(sketch, "E25.18.0.1", {"start": v(2755.9, -304.8) * mm, "end": v(2755.9, 914.4) * mm});
            skLineSegment(sketch, "E25.18.0.2", {"start": v(2755.9, 914.4) * mm, "end": v(2705.1, 914.4) * mm});
            skLineSegment(sketch, "E25.18.0.3", {"start": v(2755.9, -304.8) * mm, "end": v(2705.1, -304.8) * mm});
            skLineSegment(sketch, "E25.19.0.0", {"start": v(2432.05, -304.8) * mm, "end": v(2432.05, 914.4) * mm});
            skLineSegment(sketch, "E25.19.0.1", {"start": v(2482.85, -304.8) * mm, "end": v(2482.85, 914.4) * mm});
            skLineSegment(sketch, "E25.19.0.2", {"start": v(2482.85, 914.4) * mm, "end": v(2432.05, 914.4) * mm});
            skLineSegment(sketch, "E25.19.0.3", {"start": v(2482.85, -304.8) * mm, "end": v(2432.05, -304.8) * mm});
            skLineSegment(sketch, "E25.20.0.0", {"start": v(2159, -304.8) * mm, "end": v(2159, 914.4) * mm});
            skLineSegment(sketch, "E25.20.0.1", {"start": v(2209.8, -304.8) * mm, "end": v(2209.8, 914.4) * mm});
            skLineSegment(sketch, "E25.20.0.2", {"start": v(2209.8, 914.4) * mm, "end": v(2159, 914.4) * mm});
            skLineSegment(sketch, "E25.20.0.3", {"start": v(2209.8, -304.8) * mm, "end": v(2159, -304.8) * mm});
            skLineSegment(sketch, "E25.21.0.0", {"start": v(1885.95, -304.8) * mm, "end": v(1885.95, 914.4) * mm});
            skLineSegment(sketch, "E25.21.0.1", {"start": v(1936.75, -304.8) * mm, "end": v(1936.75, 914.4) * mm});
            skLineSegment(sketch, "E25.21.0.2", {"start": v(1936.75, 914.4) * mm, "end": v(1885.95, 914.4) * mm});
            skLineSegment(sketch, "E25.21.0.3", {"start": v(1936.75, -304.8) * mm, "end": v(1885.95, -304.8) * mm});
            skLineSegment(sketch, "E25.22.0.0", {"start": v(1612.9, -304.8) * mm, "end": v(1612.9, 914.4) * mm});
            skLineSegment(sketch, "E25.22.0.1", {"start": v(1663.7, -304.8) * mm, "end": v(1663.7, 914.4) * mm});
            skLineSegment(sketch, "E25.22.0.2", {"start": v(1663.7, 914.4) * mm, "end": v(1612.9, 914.4) * mm});
            skLineSegment(sketch, "E25.22.0.3", {"start": v(1663.7, -304.8) * mm, "end": v(1612.9, -304.8) * mm});
            skLineSegment(sketch, "E25.23.0.0", {"start": v(1339.85, -304.8) * mm, "end": v(1339.85, 914.4) * mm});
            skLineSegment(sketch, "E25.23.0.1", {"start": v(1390.65, -304.8) * mm, "end": v(1390.65, 914.4) * mm});
            skLineSegment(sketch, "E25.23.0.2", {"start": v(1390.65, 914.4) * mm, "end": v(1339.85, 914.4) * mm});
            skLineSegment(sketch, "E25.23.0.3", {"start": v(1390.65, -304.8) * mm, "end": v(1339.85, -304.8) * mm});
            skLineSegment(sketch, "E25.24.0.0", {"start": v(1066.8, -304.8) * mm, "end": v(1066.8, 914.4) * mm});
            skLineSegment(sketch, "E25.24.0.1", {"start": v(1117.6, -304.8) * mm, "end": v(1117.6, 914.4) * mm});
            skLineSegment(sketch, "E25.24.0.2", {"start": v(1117.6, 914.4) * mm, "end": v(1066.8, 914.4) * mm});
            skLineSegment(sketch, "E25.24.0.3", {"start": v(1117.6, -304.8) * mm, "end": v(1066.8, -304.8) * mm});
            skLineSegment(sketch, "E25.25.0.0", {"start": v(793.75, -304.8) * mm, "end": v(793.75, 914.4) * mm});
            skLineSegment(sketch, "E25.25.0.1", {"start": v(844.55, -304.8) * mm, "end": v(844.55, 914.4) * mm});
            skLineSegment(sketch, "E25.25.0.2", {"start": v(844.55, 914.4) * mm, "end": v(793.75, 914.4) * mm});
            skLineSegment(sketch, "E25.25.0.3", {"start": v(844.55, -304.8) * mm, "end": v(793.75, -304.8) * mm});
            skLineSegment(sketch, "E25.26.0.0", {"start": v(520.7, -304.8) * mm, "end": v(520.7, 914.4) * mm});
            skLineSegment(sketch, "E25.26.0.1", {"start": v(571.5, -304.8) * mm, "end": v(571.5, 914.4) * mm});
            skLineSegment(sketch, "E25.26.0.2", {"start": v(571.5, 914.4) * mm, "end": v(520.7, 914.4) * mm});
            skLineSegment(sketch, "E25.26.0.3", {"start": v(571.5, -304.8) * mm, "end": v(520.7, -304.8) * mm});
            skLineSegment(sketch, "E25.27.0.0", {"start": v(247.65, -304.8) * mm, "end": v(247.65, 914.4) * mm});
            skLineSegment(sketch, "E25.27.0.1", {"start": v(298.45, -304.8) * mm, "end": v(298.45, 914.4) * mm});
            skLineSegment(sketch, "E25.27.0.2", {"start": v(298.45, 914.4) * mm, "end": v(247.65, 914.4) * mm});
            skLineSegment(sketch, "E25.27.0.3", {"start": v(298.45, -304.8) * mm, "end": v(247.65, -304.8) * mm});
            skLineSegment(sketch, "E25.28.0.0", {"start": v(-25.4, -304.8) * mm, "end": v(-25.4, 914.4) * mm});
            skLineSegment(sketch, "E25.28.0.1", {"start": v(25.4, -304.8) * mm, "end": v(25.4, 914.4) * mm});
            skLineSegment(sketch, "E25.28.0.2", {"start": v(25.4, 914.4) * mm, "end": v(-25.4, 914.4) * mm});
            skLineSegment(sketch, "E25.28.0.3", {"start": v(25.4, -304.8) * mm, "end": v(-25.4, -304.8) * mm});
            skLineSegment(sketch, "E25.29.0.0", {"start": v(-298.45, -304.8) * mm, "end": v(-298.45, 914.4) * mm});
            skLineSegment(sketch, "E25.29.0.1", {"start": v(-247.65, -304.8) * mm, "end": v(-247.65, 914.4) * mm});
            skLineSegment(sketch, "E25.29.0.2", {"start": v(-247.65, 914.4) * mm, "end": v(-298.45, 914.4) * mm});
            skLineSegment(sketch, "E25.29.0.3", {"start": v(-247.65, -304.8) * mm, "end": v(-298.45, -304.8) * mm});
            skLineSegment(sketch, "E25.direction1", {"start": v(7620, -304.8) * mm, "end": v(7346.95, -304.8) * mm, "construction": true});
            skLineSegment(sketch, "E26.MirrorCS", {"start": v(-7670.8, -304.8) * mm, "end": v(-7620, -304.8) * mm});
            skLineSegment(sketch, "E27.MirrorCS", {"start": v(-7670.8, 914.4) * mm, "end": v(-7620, 914.4) * mm});
            skLineSegment(sketch, "E28.MirrorCS", {"start": v(-7620, -304.8) * mm, "end": v(-7620, 914.4) * mm});
            skLineSegment(sketch, "E29.MirrorCS", {"start": v(-7670.8, -304.8) * mm, "end": v(-7670.8, 914.4) * mm});
            skLineSegment(sketch, "E30.MirrorCS", {"start": v(-7397.75, -304.8) * mm, "end": v(-7397.75, 914.4) * mm});
            skSolve(sketch);
        }
        {
            var Q0;
            Q0=makeQuery(id+"FwvgZci3MhhO1J3_2.opExtrude","SWEPT_FACE",FACE,{"disambiguationData":[OSD([sQuery(id+"F13.wireOp",EDGE,"E25.12.0.2")])]});
            var sketch = newSketch(context, id + "F15", { "sketchPlane" : qUnion([Q0])});
            skLineSegment(sketch, "E31.bottom", {"start": v(7670.8, -5384.8) * mm, "end": v(-298.45, -5384.8) * mm});
            skLineSegment(sketch, "E31.top", {"start": v(7670.8, -5334) * mm, "end": v(-298.45, -5334) * mm});
            skLineSegment(sketch, "E31.left", {"start": v(7670.8, -5384.8) * mm, "end": v(7670.8, -5334) * mm});
            skLineSegment(sketch, "E31.right", {"start": v(-298.45, -5384.8) * mm, "end": v(-298.45, -5334) * mm});
            skLineSegment(sketch, "E32.bottom", {"start": v(7670.8, -5334) * mm, "end": v(7620, -5334) * mm});
            skLineSegment(sketch, "E32.top", {"start": v(7670.8, 5365.75) * mm, "end": v(7620, 5365.75) * mm});
            skLineSegment(sketch, "E32.left", {"start": v(7670.8, -5334) * mm, "end": v(7670.8, 5365.75) * mm});
            skLineSegment(sketch, "E32.right", {"start": v(7620, -5334) * mm, "end": v(7620, 5365.75) * mm});
            skPoint(sketch, "E33.oppositeSnap0", {"position": v(7645.4, 5365.75) * mm});
            skLineSegment(sketch, "E33.bottom", {"start": v(7670.8, 5416.55) * mm, "end": v(-298.45, 5416.55) * mm});
            skLineSegment(sketch, "E33.top", {"start": v(7670.8, 5365.75) * mm, "end": v(-298.45, 5365.75) * mm});
            skLineSegment(sketch, "E33.left", {"start": v(7670.8, 5416.55) * mm, "end": v(7670.8, 5365.75) * mm});
            skLineSegment(sketch, "E33.right", {"start": v(-298.45, 5416.55) * mm, "end": v(-298.45, 5365.75) * mm});
            skSolve(sketch);
        }
        {
            var Q0;
            Q0=makeQuery(id+"F3.boolean.opBoolean","MERGE",FACE,{"derivedFrom":[makeQuery(id+"F1.opExtrude","SWEPT_FACE",FACE,{"disambiguationData":[OSD([sQuery(id+"F0.wireOp",EDGE,"E0")])]}),makeQuery(id+"F3.opExtrude","CAP_FACE",FACE,{"disambiguationData":[OSD([sQuery(id+"F2.wireOp",EDGE,"E4.bottom"),sQuery(id+"F2.wireOp",EDGE,"E4.top"),sQuery(id+"F2.wireOp",EDGE,"E4.left"),sQuery(id+"F2.wireOp",EDGE,"E4.right")])],"isStart":true})]});
            var sketch = newSketch(context, id + "F16", { "sketchPlane" : qUnion([Q0])});
            skArc(sketch, "E34", {"start": v(7620, -5334) * mm, "mid": v(9111.83, 0) * mm, "end": v(7620, 5334) * mm});
            skLineSegment(sketch, "E35", {"start": v(7620, -5334) * mm, "end": v(7620, 5334) * mm});
            skSolve(sketch);
        }
        {
            var Q0;
            Q0 = qSketchRegion(id + "F16", true);
            extrude(context, id + "F17", {"entities" : qUnion([Q0]), "oppositeDirection" : true, "depth" : 279.4 * mm});
        }
        {
            var Q0;
            Q0=makeQuery(id+"F3.boolean.opBoolean","MERGE",FACE,{"derivedFrom":[makeQuery(id+"F1.opExtrude","SWEPT_FACE",FACE,{"disambiguationData":[OSD([sQuery(id+"F0.wireOp",EDGE,"E0")])]}),makeQuery(id+"F3.opExtrude","CAP_FACE",FACE,{"disambiguationData":[OSD([sQuery(id+"F2.wireOp",EDGE,"E4.bottom"),sQuery(id+"F2.wireOp",EDGE,"E4.top"),sQuery(id+"F2.wireOp",EDGE,"E4.left"),sQuery(id+"F2.wireOp",EDGE,"E4.right")])],"isStart":true})]});
            var sketch = newSketch(context, id + "F18", { "sketchPlane" : qUnion([Q0])});
            skLineSegment(sketch, "E36", {"start": v(-4044.06, -3864.72) * mm, "end": v(-1946.19, 0) * mm});
            skLineSegment(sketch, "E37", {"start": v(-1946.19, 0) * mm, "end": v(-4044.06, 3864.72) * mm});
            skLineSegment(sketch, "E38", {"start": v(-4044.06, 3864.72) * mm, "end": v(-4044.06, -3864.72) * mm});
            skSolve(sketch);
        }
        {
            var Q0;
            Q0 = qSketchRegion(id + "F18", true);
            extrude(context, id + "F19", {"entities" : qUnion([Q0]), "operationType" : NewBodyOperationType.REMOVE, "endBound" : BoundingType.SYMMETRIC, "oppositeDirection" : true, "depth" : 558.8 * mm});
        }
    });
